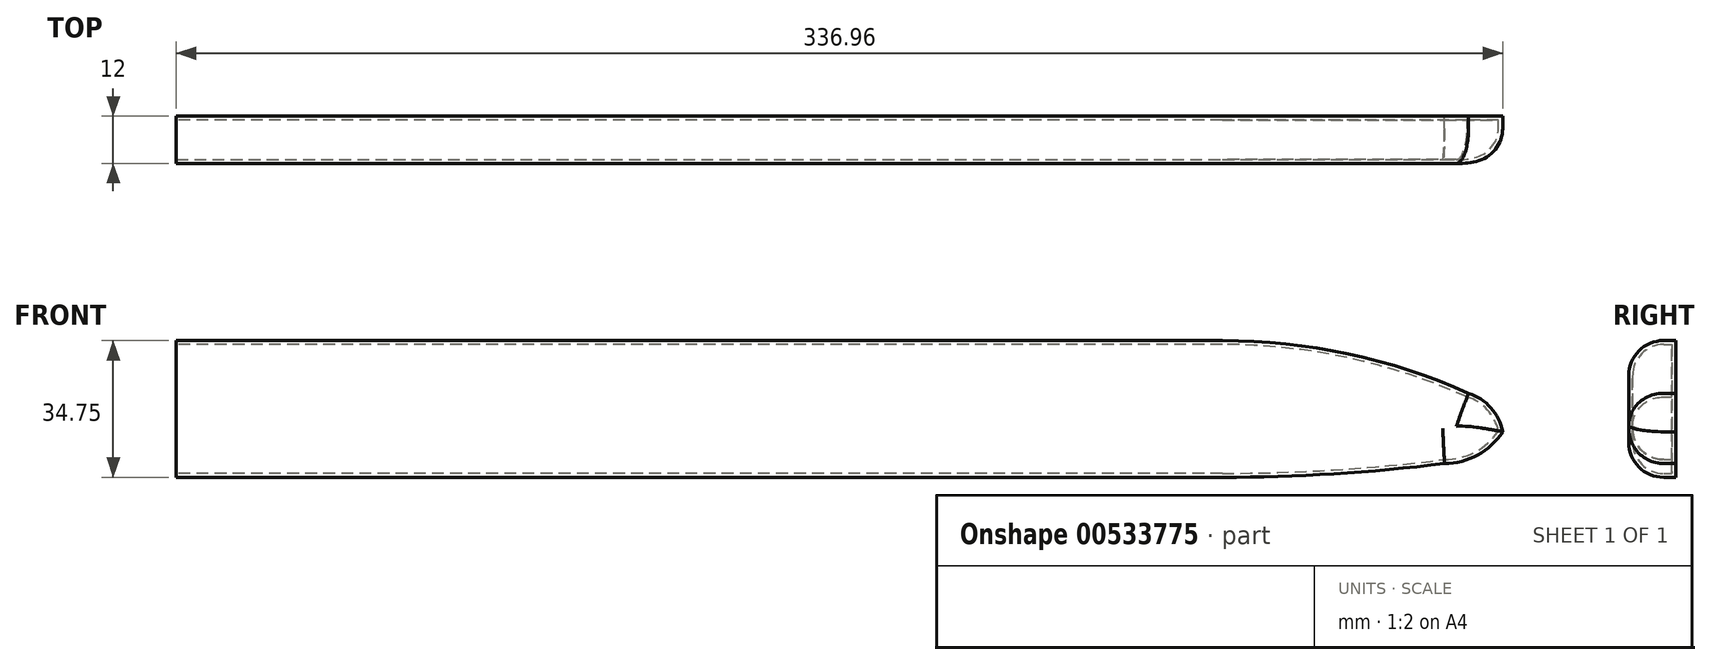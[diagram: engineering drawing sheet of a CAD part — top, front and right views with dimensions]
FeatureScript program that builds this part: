
annotation { "Feature Type Name" : "Feature", "Feature Type Description" : "" }
export const myFeature = defineFeature(function(context is Context, id is Id, definition is map)
    precondition{}
    {
        {
            var Q0;
            Q0=qCreatedBy(makeId("Front.planeOp"),FACE);
            var sketch = newSketch(context, id + "F0", { "sketchPlane" : qUnion([Q0])});
            skLineSegment(sketch, "E0.bottom", {"start": v(53.9, 25.36) * mm, "end": v(-211.85, 25.36) * mm});
            skLineSegment(sketch, "E0.top", {"start": v(53.9, -9.4) * mm, "end": v(-211.85, -9.4) * mm});
            skLineSegment(sketch, "E0.left", {"start": v(53.9, 25.36) * mm, "end": v(53.9, -9.4) * mm});
            skLineSegment(sketch, "E0.right", {"start": v(-211.85, 25.36) * mm, "end": v(-211.85, -9.4) * mm});
            skArc(sketch, "E1", {"start": v(116.44, 11.97) * mm, "mid": v(85.88, 21.97) * mm, "end": v(53.9, 25.36) * mm});
            skArc(sketch, "E2", {"start": v(53.9, -9.4) * mm, "mid": v(82.18, -8.51) * mm, "end": v(110.35, -5.88) * mm});
            skArc(sketch, "E3", {"start": v(110.35, -5.88) * mm, "mid": v(118.76, -3.73) * mm, "end": v(125.1, 2.19) * mm});
            skArc(sketch, "E4", {"start": v(125.1, 2.19) * mm, "mid": v(122.11, 8.27) * mm, "end": v(116.44, 11.97) * mm});
            skSolve(sketch);
        }
        {
            var Q0;
            Q0 = qSketchRegion(id + "F0", true);
            extrude(context, id + "F1", {"entities" : qUnion([Q0]), "depth" : 12 * mm, "offsetDistance" : 25 * mm});
        }
        {
            var Q0;
            Q0=makeQuery(id+"F1.opExtrude","CAP_EDGE",EDGE,{"disambiguationData":[OSD([sQuery(id+"F0.wireOp",EDGE,"E0.bottom")])],"isStart":false});
            var Q1;
            Q1=makeQuery(id+"F1.opExtrude","CAP_EDGE",EDGE,{"disambiguationData":[OSD([sQuery(id+"F0.wireOp",EDGE,"E4")])],"isStart":false});
            var Q2;
            Q2=makeQuery(id+"F1.opExtrude","CAP_EDGE",EDGE,{"disambiguationData":[OSD([sQuery(id+"F0.wireOp",EDGE,"E3")])],"isStart":false});
            var Q3;
            Q3=makeQuery(id+"F1.opExtrude","CAP_EDGE",EDGE,{"disambiguationData":[OSD([sQuery(id+"F0.wireOp",EDGE,"E2")])],"isStart":false});
            var Q4;
            Q4=makeQuery(id+"F1.opExtrude","CAP_EDGE",EDGE,{"disambiguationData":[OSD([sQuery(id+"F0.wireOp",EDGE,"E1")])],"isStart":false});
            fillet(context, id + "F2", {"entities" : qUnion([Q0, Q1, Q2, Q3, Q4]), "radius" : 8.9 * mm, "tangentPropagation" : true, "allowEdgeOverflow" : false});
        }
        {
            var Q0;
            Q0=makeQuery(id+"F1.opExtrude","SWEPT_FACE",FACE,{"disambiguationData":[OSD([sQuery(id+"F0.wireOp",EDGE,"E0.right")])]});
            shell(context, id + "F3", {"entities" : qUnion([Q0]), "thickness" : 1 * mm});
        }
    });
